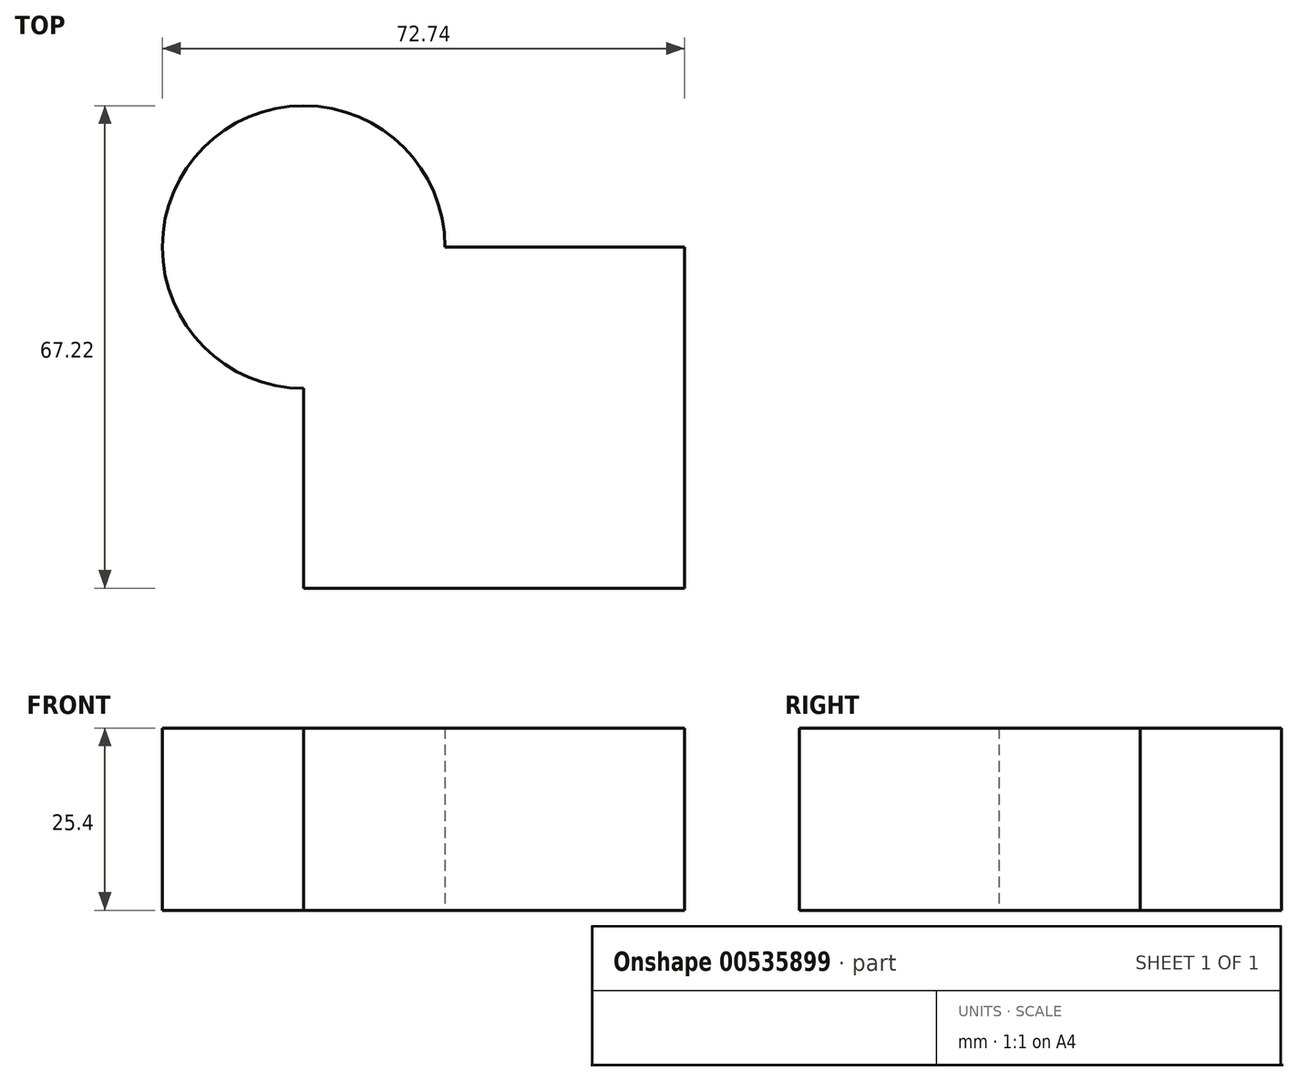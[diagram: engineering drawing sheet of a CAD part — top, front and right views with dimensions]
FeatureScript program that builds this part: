
annotation { "Feature Type Name" : "Feature", "Feature Type Description" : "" }
export const myFeature = defineFeature(function(context is Context, id is Id, definition is map)
    precondition{}
    {
        {
            var Q0;
            Q0=qCreatedBy(makeId("Top.planeOp"),FACE);
            var sketch = newSketch(context, id + "F0", { "sketchPlane" : qUnion([Q0])});
            skLineSegment(sketch, "E0.bottom", {"start": v(0, 0) * mm, "end": v(53.05, 0) * mm});
            skLineSegment(sketch, "E0.top", {"start": v(0, -47.53) * mm, "end": v(53.05, -47.53) * mm});
            skLineSegment(sketch, "E0.left", {"start": v(0, 0) * mm, "end": v(0, -47.53) * mm});
            skLineSegment(sketch, "E0.right", {"start": v(53.05, 0) * mm, "end": v(53.05, -47.53) * mm});
            skCircle(sketch, "E1", {"center": v(0, 0) * mm, "radius": 19.7 * mm});
            skSolve(sketch);
        }
        {
            var Q0;
            Q0 = qSketchRegion(id + "F0", true);
            extrude(context, id + "F1", {"entities" : qUnion([Q0]), "depth" : 25.4 * mm, "offsetDistance" : 25.4 * mm});
        }
    });
